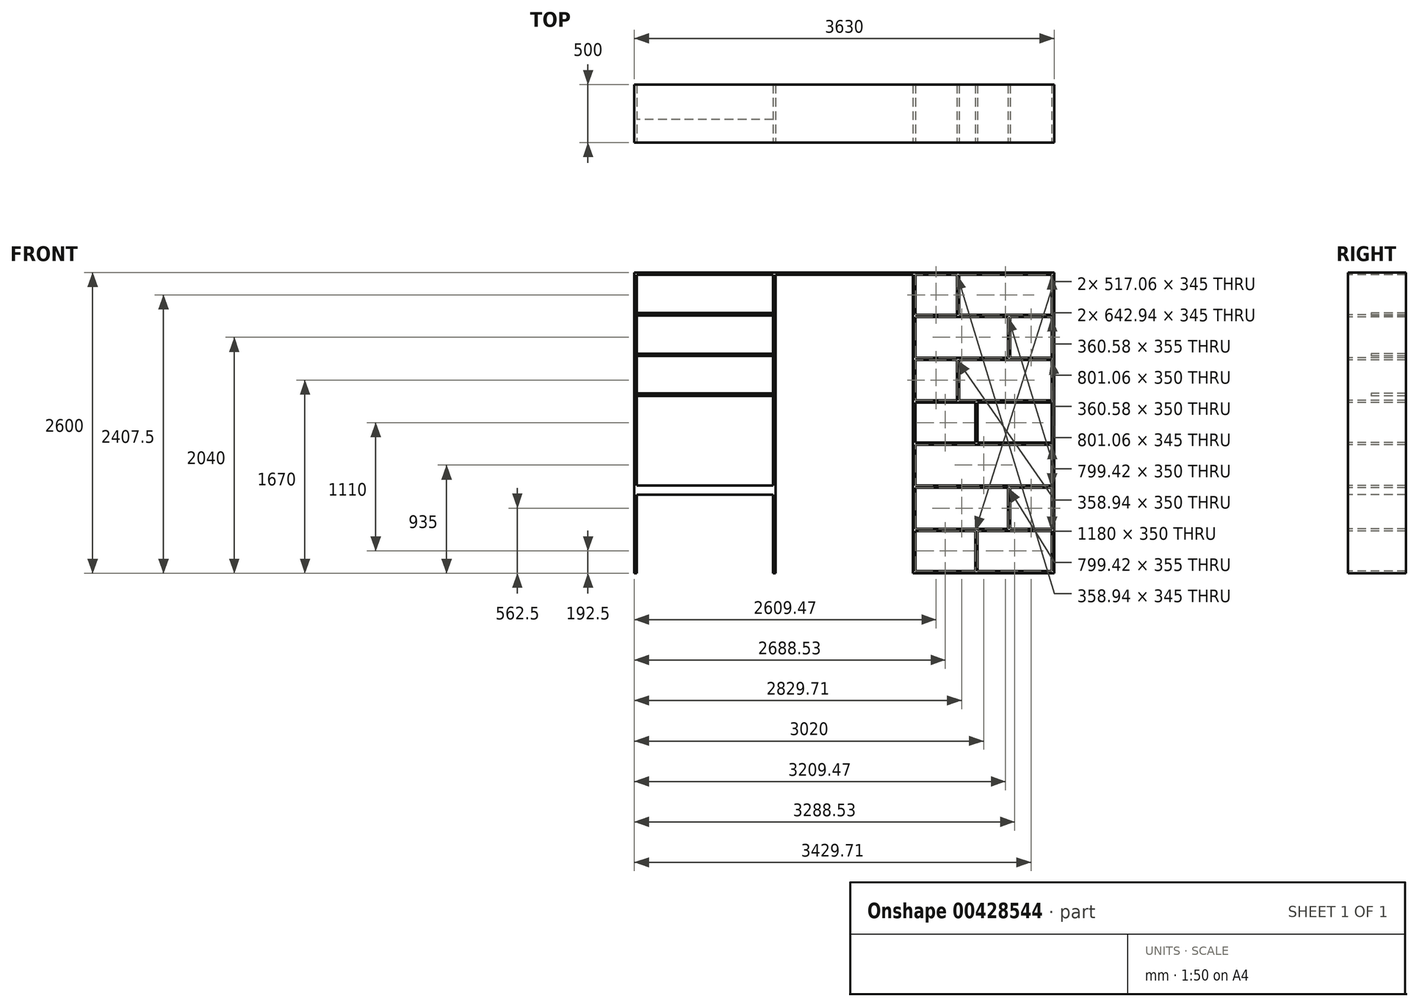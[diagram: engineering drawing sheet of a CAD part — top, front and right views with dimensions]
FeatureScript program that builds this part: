
annotation { "Feature Type Name" : "Feature", "Feature Type Description" : "" }
export const myFeature = defineFeature(function(context is Context, id is Id, definition is map)
    precondition{}
    {
        {
            var Q0;
            Q0=qCreatedBy(makeId("Front.planeOp"),FACE);
            var sketch = newSketch(context, id + "F0", { "sketchPlane" : qUnion([Q0])});
            skLineSegment(sketch, "E0.bottom", {"start": v(1815, -1300) * mm, "end": v(605, -1300) * mm});
            skLineSegment(sketch, "E0.top", {"start": v(1815, 1300) * mm, "end": v(605, 1300) * mm});
            skLineSegment(sketch, "E0.left", {"start": v(1815, -1300) * mm, "end": v(1815, 1300) * mm});
            skLineSegment(sketch, "E0.right", {"start": v(-1815, -1300) * mm, "end": v(-1815, 1300) * mm});
            skPoint(sketch, "E0.middle", {"position": v(0, 0) * mm});
            skLineSegment(sketch, "E1.0", {"start": v(595, 900) * mm, "end": v(-595, 900) * mm});
            skLineSegment(sketch, "E2.trimOffspring", {"start": v(-605, -1300) * mm, "end": v(-1815, -1300) * mm});
            skLineSegment(sketch, "E3", {"start": v(-605, -1300) * mm, "end": v(605, -1300) * mm});
            skLineSegment(sketch, "E4.0", {"start": v(-615, -620) * mm, "end": v(-1795, -620) * mm});
            skLineSegment(sketch, "E5.0", {"start": v(-615, -580) * mm, "end": v(-1795, -580) * mm});
            skLineSegment(sketch, "E6.0", {"start": v(-615, -540) * mm, "end": v(-1795, -540) * mm});
            skLineSegment(sketch, "E7.trimOffspring", {"start": v(-605, 1300) * mm, "end": v(-1815, 1300) * mm});
            skLineSegment(sketch, "E8", {"start": v(-605, 1300) * mm, "end": v(605, 1300) * mm});
            skLineSegment(sketch, "E9.0", {"start": v(-615, 950) * mm, "end": v(-1795, 950) * mm});
            skLineSegment(sketch, "E10.0", {"start": v(-615, 600) * mm, "end": v(-1795, 600) * mm});
            skLineSegment(sketch, "E11.0", {"start": v(-615, 235) * mm, "end": v(-1795, 235) * mm});
            skLineSegment(sketch, "E12.0", {"start": v(1795, -915) * mm, "end": v(1434.42, -915) * mm});
            skLineSegment(sketch, "E13.0", {"start": v(1795, -560) * mm, "end": v(1434.42, -560) * mm});
            skLineSegment(sketch, "E14.0", {"start": v(1795, -190) * mm, "end": v(615, -190) * mm});
            skLineSegment(sketch, "E15.0", {"start": v(1795, 195) * mm, "end": v(993.94, 195) * mm});
            skLineSegment(sketch, "E16.0", {"start": v(1795, 565) * mm, "end": v(1434.42, 565) * mm});
            skLineSegment(sketch, "E17.0", {"start": v(1795, 935) * mm, "end": v(993.94, 935) * mm});
            skLineSegment(sketch, "E18.0", {"start": v(-1795, -1300) * mm, "end": v(-1795, 235) * mm});
            skLineSegment(sketch, "E19.0", {"start": v(1795, -1280) * mm, "end": v(1795, -935) * mm});
            skLineSegment(sketch, "E20.0", {"start": v(-615, 1280) * mm, "end": v(-1795, 1280) * mm});
            skLineSegment(sketch, "E20.1", {"start": v(-595, 1280) * mm, "end": v(595, 1280) * mm});
            skLineSegment(sketch, "E20.2", {"start": v(1795, 1280) * mm, "end": v(993.94, 1280) * mm});
            skLineSegment(sketch, "E21.0", {"start": v(-615, 255) * mm, "end": v(-1795, 255) * mm});
            skLineSegment(sketch, "E22.0", {"start": v(-615, 580) * mm, "end": v(-1795, 580) * mm});
            skLineSegment(sketch, "E23.0", {"start": v(-615, 930) * mm, "end": v(-1795, 930) * mm});
            skLineSegment(sketch, "E24.0", {"start": v(1795, -935) * mm, "end": v(1152.06, -935) * mm});
            skLineSegment(sketch, "E25.0", {"start": v(1795, -540) * mm, "end": v(1434.42, -540) * mm});
            skLineSegment(sketch, "E26.0", {"start": v(1795, -170) * mm, "end": v(1152.06, -170) * mm});
            skLineSegment(sketch, "E27.0", {"start": v(1795, 175) * mm, "end": v(1152.06, 175) * mm});
            skLineSegment(sketch, "E28.0", {"start": v(1795, 545) * mm, "end": v(993.94, 545) * mm});
            skLineSegment(sketch, "E29.0", {"start": v(1795, 915) * mm, "end": v(1434.42, 915) * mm});
            skLineSegment(sketch, "E30.0", {"start": v(595, -1300) * mm, "end": v(595, 1280) * mm});
            skLineSegment(sketch, "E31.0", {"start": v(615, -1280) * mm, "end": v(615, -935) * mm});
            skLineSegment(sketch, "E32.0", {"start": v(-595, -1300) * mm, "end": v(-595, 1280) * mm});
            skLineSegment(sketch, "E33.0", {"start": v(-615, -1300) * mm, "end": v(-615, 235) * mm});
            skPoint(sketch, "E34.orphan", {"position": v(-1815, -540) * mm});
            skPoint(sketch, "E35.orphan", {"position": v(-1815, -620) * mm});
            skLineSegment(sketch, "E36.trimOffspring", {"start": v(-1795, 255) * mm, "end": v(-1795, 580) * mm});
            skLineSegment(sketch, "E37.trimOffspring", {"start": v(-1795, 600) * mm, "end": v(-1795, 930) * mm});
            skPoint(sketch, "E38.orphan", {"position": v(-1815, 600) * mm});
            skPoint(sketch, "E39.orphan", {"position": v(-1815, 950) * mm});
            skLineSegment(sketch, "E40.trimOffspring", {"start": v(-1795, 950) * mm, "end": v(-1795, 1280) * mm});
            skLineSegment(sketch, "E41.trimOffspring", {"start": v(-615, 600) * mm, "end": v(-615, 930) * mm});
            skLineSegment(sketch, "E42.trimOffspring", {"start": v(-615, 950) * mm, "end": v(-615, 1280) * mm});
            skLineSegment(sketch, "E43.trimOffspring", {"start": v(-615, 255) * mm, "end": v(-615, 580) * mm});
            skLineSegment(sketch, "E44.trimOffspring", {"start": v(615, -540) * mm, "end": v(615, -190) * mm});
            skLineSegment(sketch, "E45.trimOffspring", {"start": v(615, -915) * mm, "end": v(615, -560) * mm});
            skLineSegment(sketch, "E46.trimOffspring", {"start": v(1795, -915) * mm, "end": v(1795, -560) * mm});
            skLineSegment(sketch, "E47.trimOffspring", {"start": v(1795, -540) * mm, "end": v(1795, -190) * mm});
            skLineSegment(sketch, "E48.trimOffspring", {"start": v(1795, -170) * mm, "end": v(1795, 175) * mm});
            skLineSegment(sketch, "E49.trimOffspring", {"start": v(1795, 195) * mm, "end": v(1795, 545) * mm});
            skLineSegment(sketch, "E50.trimOffspring", {"start": v(615, -170) * mm, "end": v(615, 175) * mm});
            skLineSegment(sketch, "E51.trimOffspring", {"start": v(615, 195) * mm, "end": v(615, 545) * mm});
            skLineSegment(sketch, "E52.trimOffspring", {"start": v(615, 565) * mm, "end": v(615, 915) * mm});
            skLineSegment(sketch, "E53.trimOffspring", {"start": v(1795, 565) * mm, "end": v(1795, 915) * mm});
            skLineSegment(sketch, "E54.trimOffspring", {"start": v(615, 935) * mm, "end": v(615, 1280) * mm});
            skLineSegment(sketch, "E55.trimOffspring", {"start": v(1795, 935) * mm, "end": v(1795, 1280) * mm});
            skLineSegment(sketch, "E56", {"start": v(973.94, 1280) * mm, "end": v(973.94, 935) * mm});
            skLineSegment(sketch, "E57", {"start": v(1414.42, 915) * mm, "end": v(1414.42, 565) * mm});
            skLineSegment(sketch, "E58", {"start": v(1132.06, 175) * mm, "end": v(1132.06, -170) * mm});
            skLineSegment(sketch, "E59.0", {"start": v(665, -1300) * mm, "end": v(665, -1295) * mm});
            skLineSegment(sketch, "E60", {"start": v(605, -290) * mm, "end": v(810.17, -290) * mm, "construction": true});
            skLineSegment(sketch, "E61.trimOffspring", {"start": v(665, -540) * mm, "end": v(665, -170) * mm, "construction": true});
            skLineSegment(sketch, "E62.trimOffspring", {"start": v(973.94, 545) * mm, "end": v(973.94, 195) * mm});
            skLineSegment(sketch, "E63.trimOffspring", {"start": v(1414.42, -1295) * mm, "end": v(1414.42, -1300) * mm});
            skLineSegment(sketch, "E64.trimOffspring", {"start": v(1414.42, -560) * mm, "end": v(1414.42, -915) * mm});
            skLineSegment(sketch, "E65", {"start": v(1132.06, -935) * mm, "end": v(1132.06, -1280) * mm});
            skLineSegment(sketch, "E66.0", {"start": v(1434.42, -560) * mm, "end": v(1434.42, -915) * mm});
            skLineSegment(sketch, "E67.0", {"start": v(1152.06, -935) * mm, "end": v(1152.06, -1280) * mm});
            skLineSegment(sketch, "E68.0", {"start": v(1152.06, 175) * mm, "end": v(1152.06, -170) * mm});
            skLineSegment(sketch, "E69.0", {"start": v(993.94, 545) * mm, "end": v(993.94, 195) * mm});
            skLineSegment(sketch, "E70.0", {"start": v(1434.42, 915) * mm, "end": v(1434.42, 565) * mm});
            skLineSegment(sketch, "E71.0", {"start": v(993.94, 1280) * mm, "end": v(993.94, 935) * mm});
            skLineSegment(sketch, "E72.trimOffspring", {"start": v(973.94, 935) * mm, "end": v(615, 935) * mm});
            skLineSegment(sketch, "E73.trimOffspring", {"start": v(973.94, 1280) * mm, "end": v(615, 1280) * mm});
            skLineSegment(sketch, "E74.trimOffspring", {"start": v(1414.42, 915) * mm, "end": v(615, 915) * mm});
            skLineSegment(sketch, "E75.trimOffspring", {"start": v(1414.42, 565) * mm, "end": v(615, 565) * mm});
            skLineSegment(sketch, "E76.trimOffspring", {"start": v(973.94, 545) * mm, "end": v(615, 545) * mm});
            skLineSegment(sketch, "E77.trimOffspring", {"start": v(1132.06, 175) * mm, "end": v(615, 175) * mm});
            skLineSegment(sketch, "E78.trimOffspring", {"start": v(973.94, 195) * mm, "end": v(615, 195) * mm});
            skLineSegment(sketch, "E79.trimOffspring", {"start": v(1132.06, -170) * mm, "end": v(615, -170) * mm});
            skLineSegment(sketch, "E80.trimOffspring", {"start": v(1414.42, -540) * mm, "end": v(615, -540) * mm});
            skLineSegment(sketch, "E81.trimOffspring", {"start": v(1414.42, -915) * mm, "end": v(615, -915) * mm});
            skLineSegment(sketch, "E82.trimOffspring", {"start": v(1132.06, -935) * mm, "end": v(615, -935) * mm});
            skLineSegment(sketch, "E83.trimOffspring", {"start": v(1414.42, -560) * mm, "end": v(615, -560) * mm});
            skLineSegment(sketch, "E84", {"start": v(1434.42, -540) * mm, "end": v(1414.42, -540) * mm});
            skLineSegment(sketch, "E85", {"start": v(-615, 950) * mm, "end": v(-615, 930) * mm});
            skLineSegment(sketch, "E86", {"start": v(-615, 600) * mm, "end": v(-615, 580) * mm});
            skLineSegment(sketch, "E87", {"start": v(-615, 255) * mm, "end": v(-615, 235) * mm});
            skLineSegment(sketch, "E88", {"start": v(-1795, 255) * mm, "end": v(-1795, 235) * mm});
            skLineSegment(sketch, "E89", {"start": v(-1795, 600) * mm, "end": v(-1795, 580) * mm});
            skLineSegment(sketch, "E90", {"start": v(-1795, 950) * mm, "end": v(-1795, 930) * mm});
            skLineSegment(sketch, "E91.0", {"start": v(1795, -1280) * mm, "end": v(615, -1280) * mm});
            skSolve(sketch);
        }
        {
            var Q0;
            Q0=makeQuery(id+"F0.imprint","IMPRINT",FACE,{"disambiguationData":[TD([[makeQuery(id+"F0.imprint","IMPRINT",EDGE,{"derivedFrom":sQuery(id+"F0.wireOp",EDGE,"E0.top")}),1.0]])]});
            extrude(context, id + "F1", {"entities" : qUnion([Q0]), "depth" : -500 * mm});
        }
        {
            var Q0;
            {var subQ0=sQuery(id+"F0.wireOp",EDGE,"E5.0");Q0=makeQuery(id+"F0.imprint","IMPRINT",FACE,{"disambiguationData":[TD([[makeQuery(id+"F0.imprint","IMPRINT",EDGE,{"derivedFrom":subQ0}),-1.0]])]});}
            extrude(context, id + "F2", {"entities" : qUnion([Q0]), "operationType" : NewBodyOperationType.ADD, "depth" : -500 * mm});
        }
        {
            var Q0;
            {var subQ0=sQuery(id+"F0.wireOp",EDGE,"E4.0");Q0=makeQuery(id+"F0.imprint","IMPRINT",FACE,{"disambiguationData":[TD([[makeQuery(id+"F0.imprint","IMPRINT",EDGE,{"derivedFrom":subQ0}),-1.0]])]});}
            extrude(context, id + "F3", {"entities" : qUnion([Q0]), "operationType" : NewBodyOperationType.ADD, "depth" : -500 * mm});
        }
        {
            var Q0;
            Q0=makeQuery(id+"F0.imprint","IMPRINT",FACE,{"disambiguationData":[TD([[makeQuery(id+"F0.imprint","IMPRINT",EDGE,{"derivedFrom":sQuery(id+"F0.wireOp",EDGE,"E11.0")}),-1.0]])]});
            var Q1;
            Q1=makeQuery(id+"F0.imprint","IMPRINT",FACE,{"disambiguationData":[TD([[makeQuery(id+"F0.imprint","IMPRINT",EDGE,{"derivedFrom":sQuery(id+"F0.wireOp",EDGE,"E10.0")}),1.0]])]});
            var Q2;
            Q2=makeQuery(id+"F0.imprint","IMPRINT",FACE,{"disambiguationData":[TD([[makeQuery(id+"F0.imprint","IMPRINT",EDGE,{"derivedFrom":sQuery(id+"F0.wireOp",EDGE,"E9.0")}),1.0]])]});
            extrude(context, id + "F4", {"entities" : qUnion([Q0, Q1, Q2]), "operationType" : NewBodyOperationType.ADD, "oppositeDirection" : true, "depth" : 500 * mm, "hasSecondDirection" : true, "secondDirectionOppositeDirection" : true, "secondDirectionDepth" : 200 * mm});
        }
    });
